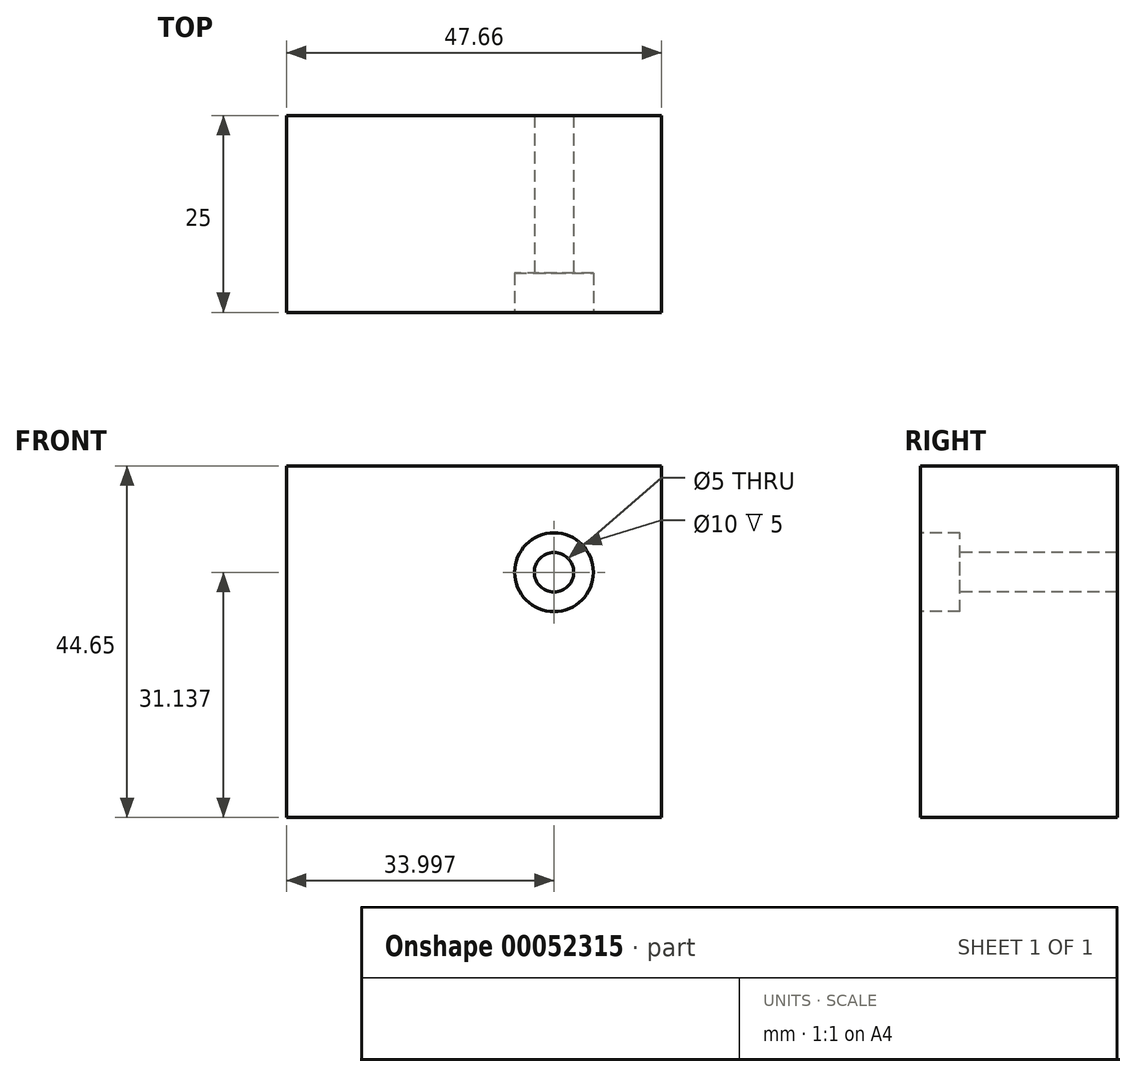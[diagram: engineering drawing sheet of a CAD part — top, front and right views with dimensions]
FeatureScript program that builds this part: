
annotation { "Feature Type Name" : "Feature", "Feature Type Description" : "" }
export const myFeature = defineFeature(function(context is Context, id is Id, definition is map)
    precondition{}
    {
        {
            var Q0;
            Q0=qCreatedBy(makeId("Front.planeOp"),FACE);
            var sketch = newSketch(context, id + "F0", { "sketchPlane" : qUnion([Q0])});
            skLineSegment(sketch, "E0.bottom", {"start": v(0, 0) * mm, "end": v(47.66, 0) * mm});
            skLineSegment(sketch, "E0.top", {"start": v(0, 44.65) * mm, "end": v(47.66, 44.65) * mm});
            skLineSegment(sketch, "E0.left", {"start": v(0, 0) * mm, "end": v(0, 44.65) * mm});
            skLineSegment(sketch, "E0.right", {"start": v(47.66, 0) * mm, "end": v(47.66, 44.65) * mm});
            skSolve(sketch);
        }
        {
            var Q0;
            Q0=makeQuery(id+"F0.imprint","IMPRINT",FACE,{"disambiguationData":[TD([[makeQuery(id+"F0.imprint","IMPRINT",EDGE,{"derivedFrom":sQuery(id+"F0.wireOp",EDGE,"E0.bottom")}),1.0]])]});
            extrude(context, id + "F1", {"entities" : qUnion([Q0]), "depth" : 25 * mm});
        }
        {
            var Q0;
            Q0=makeQuery(id+"F1.opExtrude","CAP_FACE",FACE,{"disambiguationData":[OSD([sQuery(id+"F0.wireOp",EDGE,"E0.bottom"),sQuery(id+"F0.wireOp",EDGE,"E0.top"),sQuery(id+"F0.wireOp",EDGE,"E0.left"),sQuery(id+"F0.wireOp",EDGE,"E0.right")])],"isStart":false});
            var sketch = newSketch(context, id + "F2", { "sketchPlane" : qUnion([Q0])});
            skCircle(sketch, "E1", {"center": v(34, 31.14) * mm, "radius": 5.82 * mm});
            skSolve(sketch);
        }
        {
            var Q0;
            Q0=sQuery(id+"F2.wireOp",VERTEX,"E1.center");
            var Q1;
            Q1=makeQuery(id+"F1.opExtrude","SWEPT_BODY",BODY,{"disambiguationData":[OSD([sQuery(id+"F0.wireOp",EDGE,"E0.bottom"),sQuery(id+"F0.wireOp",EDGE,"E0.top"),sQuery(id+"F0.wireOp",EDGE,"E0.left"),sQuery(id+"F0.wireOp",EDGE,"E0.right")])]});
            hole(context, id + "F3", {"style" : HoleStyle.C_BORE, "holeDiameter" : 5 * mm, "cBoreDiameter" : 10 * mm, "cBoreDepth" : 5 * mm, "endStyle" : HoleEndStyle.THROUGH, "locations" : qUnion([Q0]), "scope" : qUnion([Q1])});
        }
    });
